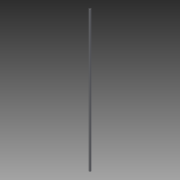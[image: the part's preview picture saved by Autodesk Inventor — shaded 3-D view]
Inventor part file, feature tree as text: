
AUTODESK INVENTOR PART (.ipt)
format: ipt  version: 2015 SP1 (Build 190203100, 203)  size: 74,752 bytes
history: native  units: mm
features: extrude x1, sketch x1
ambient origin geometry x8: Origin, YZ Plane, XZ Plane, XY Plane, X Axis, Y Axis, Z Axis, Center Point
bodies: Solid1 (feature_tree)
feature tree (2):
  extrude  "Extrusion1"  Depth=20.0mm
  sketch  "Sketch1"  dims[d0=20.0mm d1=20.0mm d2=2.0mm d3=2200.0mm d4=0.0mm]
